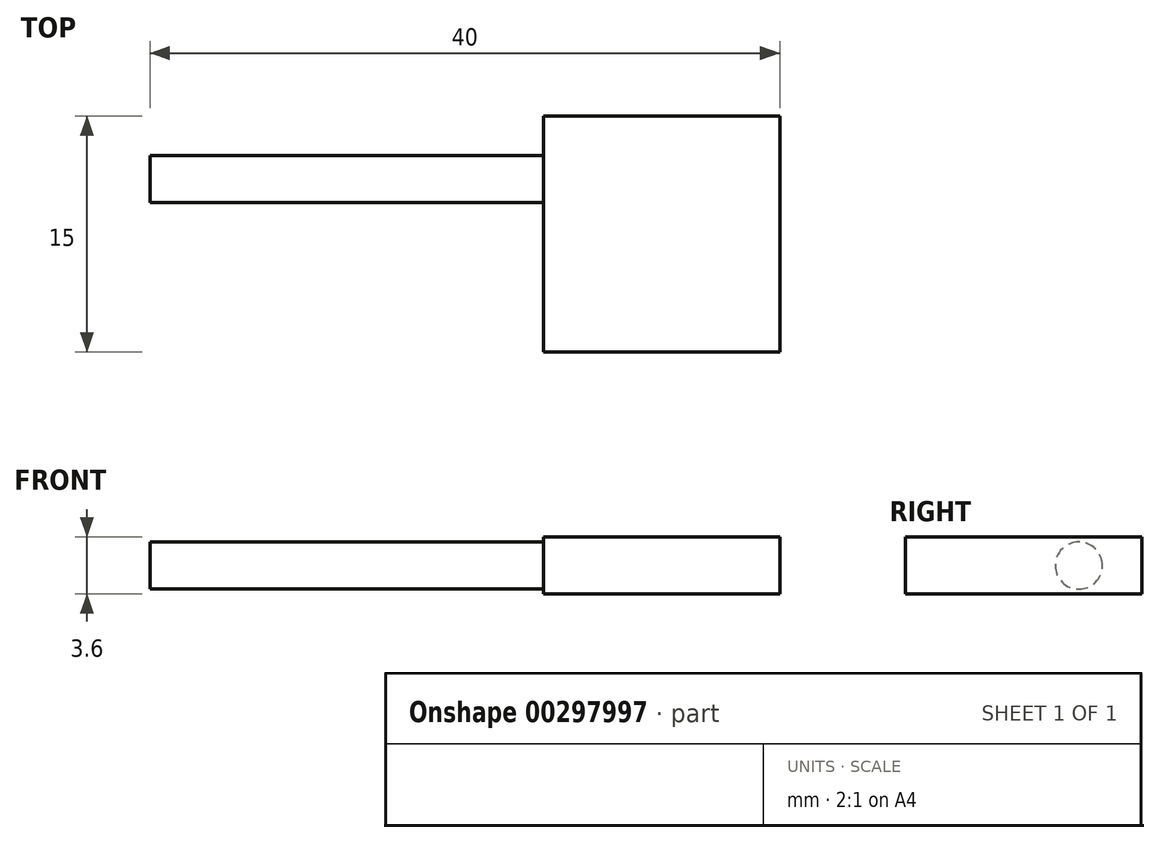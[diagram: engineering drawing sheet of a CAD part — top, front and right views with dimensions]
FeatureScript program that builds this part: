
annotation { "Feature Type Name" : "Feature", "Feature Type Description" : "" }
export const myFeature = defineFeature(function(context is Context, id is Id, definition is map)
    precondition{}
    {
        {
            var Q0;
            Q0=qCreatedBy(makeId("Top.planeOp"),FACE);
            var sketch = newSketch(context, id + "F0", { "sketchPlane" : qUnion([Q0])});
            skLineSegment(sketch, "E0.bottom", {"start": v(7.5, 7.5) * mm, "end": v(-7.5, 7.5) * mm});
            skLineSegment(sketch, "E0.top", {"start": v(7.5, -7.5) * mm, "end": v(-7.5, -7.5) * mm});
            skLineSegment(sketch, "E0.left", {"start": v(7.5, 7.5) * mm, "end": v(7.5, -7.5) * mm});
            skLineSegment(sketch, "E0.right", {"start": v(-7.5, 7.5) * mm, "end": v(-7.5, -7.5) * mm});
            skPoint(sketch, "E0.middle", {"position": v(0, 0) * mm});
            skSolve(sketch);
        }
        {
            var Q0;
            Q0=makeQuery(id+"F0.imprint","IMPRINT",FACE,{"disambiguationData":[TD([[makeQuery(id+"F0.imprint","IMPRINT",EDGE,{"derivedFrom":sQuery(id+"F0.wireOp",EDGE,"E0.bottom")}),1.0]])]});
            extrude(context, id + "F1", {"entities" : qUnion([Q0]), "depth" : 3.6 * mm});
        }
        {
            var Q0;
            Q0=makeQuery(id+"F1.opExtrude","SWEPT_FACE",FACE,{"disambiguationData":[OSD([sQuery(id+"F0.wireOp",EDGE,"E0.right")])]});
            var sketch = newSketch(context, id + "F2", { "sketchPlane" : qUnion([Q0])});
            skCircle(sketch, "E1", {"center": v(-3.5, 1.8) * mm, "radius": 1.5 * mm});
            skPoint(sketch, "E1.centerSnap0", {"position": v(-7.5, 1.8) * mm});
            skSolve(sketch);
        }
        {
            var Q0;
            Q0=makeQuery(id+"F2.imprint","IMPRINT",FACE,{"disambiguationData":[TD([[makeQuery(id+"F2.imprint","IMPRINT",EDGE,{"derivedFrom":sQuery(id+"F2.wireOp",EDGE,"E1")}),1.0]])]});
            extrude(context, id + "F3", {"entities" : qUnion([Q0]), "operationType" : NewBodyOperationType.ADD, "depth" : 25 * mm});
        }
    });
